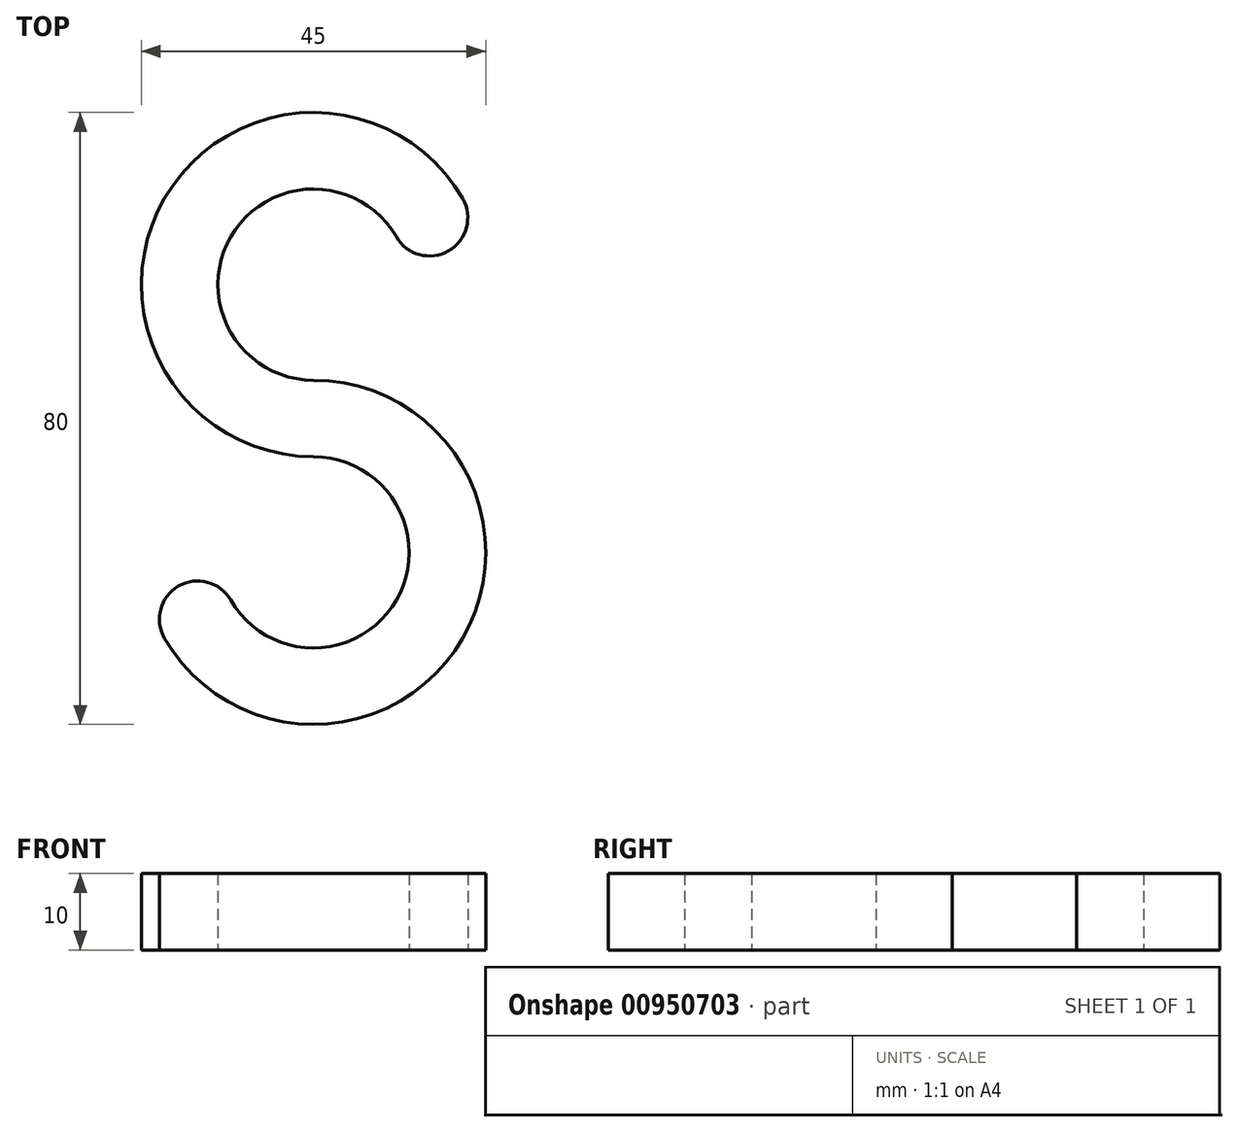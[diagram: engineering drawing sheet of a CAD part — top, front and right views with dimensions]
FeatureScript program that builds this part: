
annotation { "Feature Type Name" : "Feature", "Feature Type Description" : "" }
export const myFeature = defineFeature(function(context is Context, id is Id, definition is map)
    precondition{}
    {
        {
            var Q0;
            Q0=qCreatedBy(makeId("Top.planeOp"),FACE);
            var sketch = newSketch(context, id + "F0", { "sketchPlane" : qUnion([Q0])});
            skCircle(sketch, "E0", {"center": v(0, 17.5) * mm, "radius": 17.5 * mm, "construction": true});
            skCircle(sketch, "E1.MirrorC", {"center": v(0, -17.5) * mm, "radius": 17.5 * mm, "construction": true});
            skArc(sketch, "E2", {"start": v(0, 0) * mm, "mid": v(-15.16, 26.25) * mm, "end": v(15.16, 26.25) * mm});
            skArc(sketch, "E3", {"start": v(0, 0) * mm, "mid": v(15.16, -26.25) * mm, "end": v(-15.16, -26.25) * mm});
            skLineSegment(sketch, "E4", {"start": v(-23.4, -40.53) * mm, "end": v(31.6, 54.75) * mm, "construction": true});
            skArc(sketch, "E5.0.startCap", {"start": v(0, 5) * mm, "mid": v(5, 0) * mm, "end": v(0, -5) * mm});
            skArc(sketch, "E5.0.endCap", {"start": v(19.49, 28.75) * mm, "mid": v(17.66, 21.92) * mm, "end": v(10.83, 23.75) * mm});
            skArc(sketch, "E5.0.left", {"start": v(0, -5) * mm, "mid": v(-19.49, 28.75) * mm, "end": v(19.49, 28.75) * mm});
            skArc(sketch, "E5.0.right", {"start": v(0, 5) * mm, "mid": v(-10.83, 23.75) * mm, "end": v(10.83, 23.75) * mm});
            skArc(sketch, "E5.1.startCap", {"start": v(0, -5) * mm, "mid": v(-5, 0) * mm, "end": v(0, 5) * mm});
            skArc(sketch, "E5.1.endCap", {"start": v(-19.49, -28.75) * mm, "mid": v(-17.66, -21.92) * mm, "end": v(-10.83, -23.75) * mm});
            skArc(sketch, "E5.1.left", {"start": v(0, 5) * mm, "mid": v(19.49, -28.75) * mm, "end": v(-19.49, -28.75) * mm});
            skArc(sketch, "E5.1.right", {"start": v(0, -5) * mm, "mid": v(10.83, -23.75) * mm, "end": v(-10.83, -23.75) * mm});
            skSolve(sketch);
        }
        {
            var Q0;
            Q0 = qSketchRegion(id + "F0", true);
            extrude(context, id + "F1", {"entities" : qUnion([Q0]), "depth" : 10 * mm, "offsetDistance" : 25 * mm});
        }
    });
